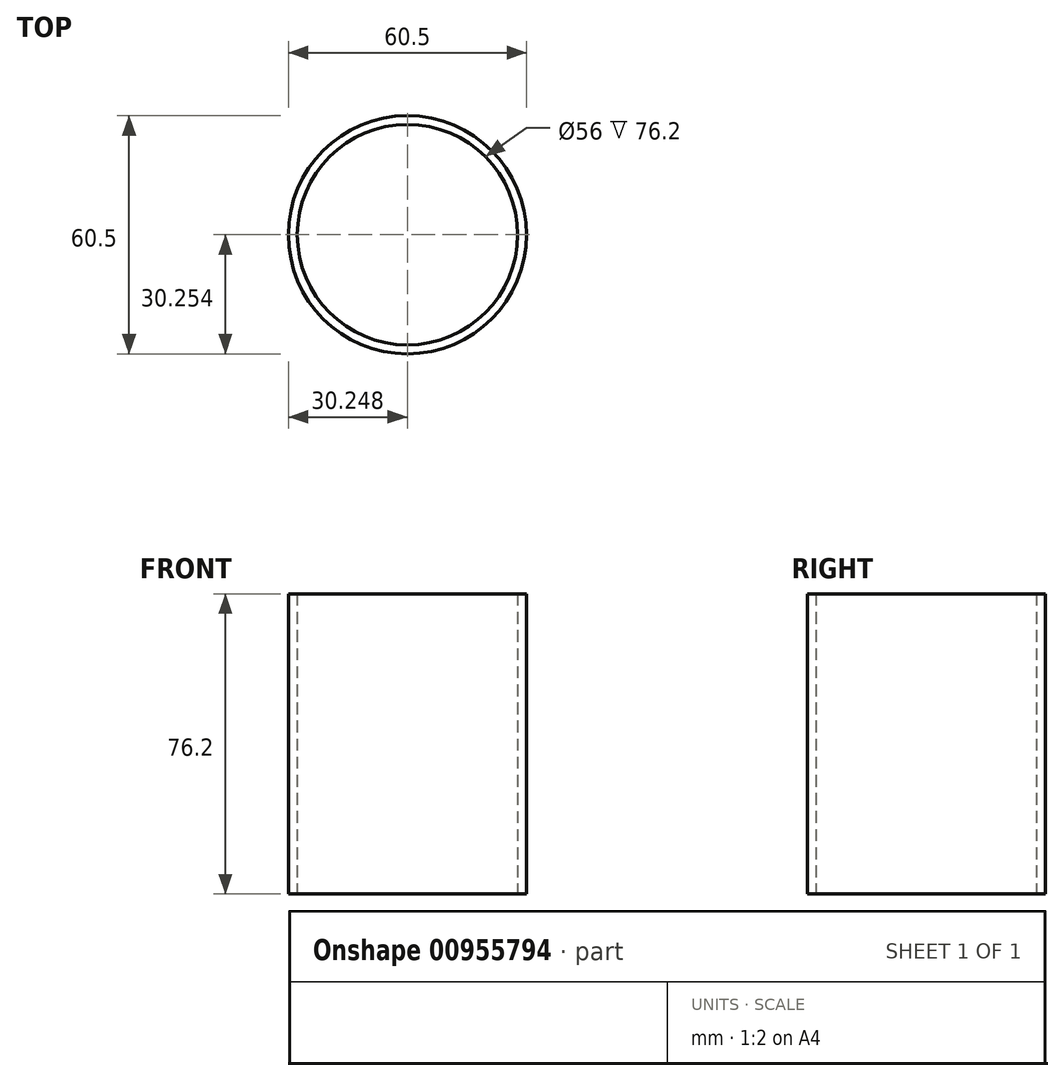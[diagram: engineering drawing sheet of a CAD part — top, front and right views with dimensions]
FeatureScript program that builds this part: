
annotation { "Feature Type Name" : "Feature", "Feature Type Description" : "" }
export const myFeature = defineFeature(function(context is Context, id is Id, definition is map)
    precondition{}
    {
        {
            var Q0;
            Q0=qCreatedBy(makeId("Top.planeOp"),FACE);
            var sketch = newSketch(context, id + "F0", { "sketchPlane" : qUnion([Q0])});
            skCircle(sketch, "E0", {"center": v(0.66, -1.54) * mm, "radius": 30.25 * mm});
            skCircle(sketch, "E1", {"center": v(0.66, -1.54) * mm, "radius": 28 * mm});
            skSolve(sketch);
        }
        {
            var Q0;
            Q0=makeQuery(id+"F0.imprint","IMPRINT",FACE,{"disambiguationData":[TD([[makeQuery(id+"F0.imprint","IMPRINT",EDGE,{"derivedFrom":sQuery(id+"F0.wireOp",EDGE,"E0")}),1.0]])]});
            extrude(context, id + "F1", {"entities" : qUnion([Q0]), "depth" : 76.2 * mm, "offsetDistance" : 25 * mm});
        }
    });
